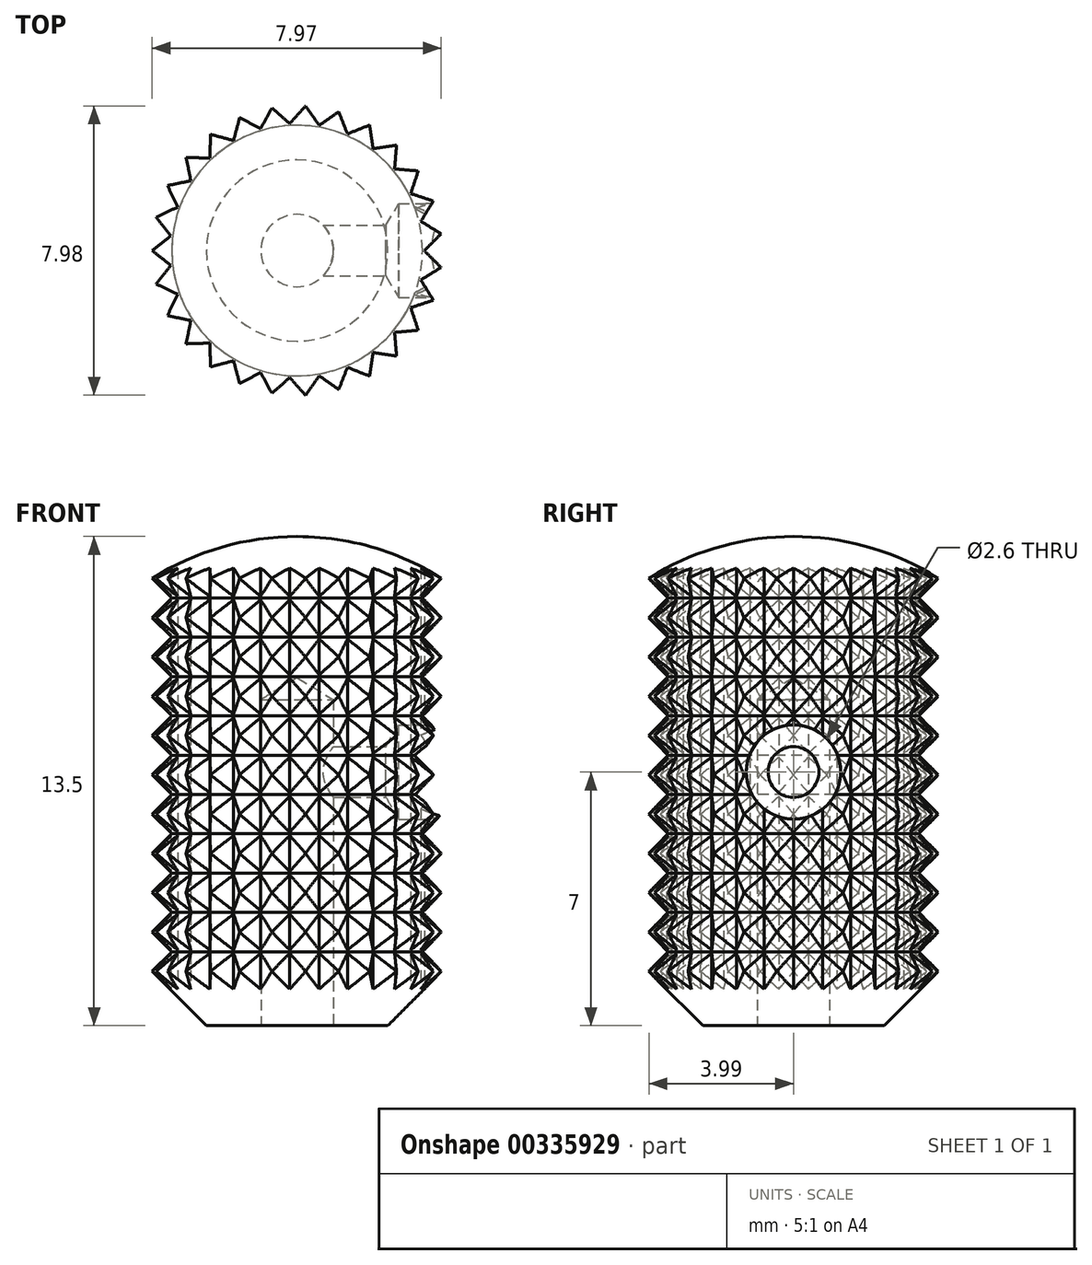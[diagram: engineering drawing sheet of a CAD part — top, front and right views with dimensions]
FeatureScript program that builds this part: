
annotation { "Feature Type Name" : "Feature", "Feature Type Description" : "" }
export const myFeature = defineFeature(function(context is Context, id is Id, definition is map)
    precondition{}
    {
        {
            var Q0;
            Q0=qCreatedBy(makeId("Top.planeOp"),FACE);
            var sketch = newSketch(context, id + "F0", { "sketchPlane" : qUnion([Q0])});
            skCircle(sketch, "E0", {"center": v(0, 0) * mm, "radius": 4 * mm, "construction": true});
            skLineSegment(sketch, "E1", {"start": v(0, 0) * mm, "end": v(4, 0) * mm, "construction": true});
            skLineSegment(sketch, "E2", {"start": v(3.5, 0) * mm, "end": v(3.97, 0.46) * mm});
            skLineSegment(sketch, "E3.MirrorCS", {"start": v(3.5, 0) * mm, "end": v(3.97, -0.46) * mm});
            skLineSegment(sketch, "E4.1.0", {"start": v(3.41, -0.8) * mm, "end": v(3.97, -0.46) * mm});
            skLineSegment(sketch, "E4.1.1", {"start": v(3.41, -0.8) * mm, "end": v(3.76, -1.37) * mm});
            skLineSegment(sketch, "E4.2.0", {"start": v(3.14, -1.57) * mm, "end": v(3.76, -1.37) * mm});
            skLineSegment(sketch, "E4.2.1", {"start": v(3.14, -1.57) * mm, "end": v(3.34, -2.2) * mm});
            skLineSegment(sketch, "E4.3.0", {"start": v(2.69, -2.26) * mm, "end": v(3.34, -2.2) * mm});
            skLineSegment(sketch, "E4.3.1", {"start": v(2.69, -2.26) * mm, "end": v(2.74, -2.9) * mm});
            skLineSegment(sketch, "E4.4.0", {"start": v(2.1, -2.81) * mm, "end": v(2.74, -2.9) * mm});
            skLineSegment(sketch, "E4.4.1", {"start": v(2.1, -2.81) * mm, "end": v(2, -3.46) * mm});
            skLineSegment(sketch, "E4.5.0", {"start": v(1.39, -3.22) * mm, "end": v(2, -3.46) * mm});
            skLineSegment(sketch, "E4.5.1", {"start": v(1.39, -3.22) * mm, "end": v(1.15, -3.83) * mm});
            skLineSegment(sketch, "E4.6.0", {"start": v(0.6, -3.46) * mm, "end": v(1.15, -3.83) * mm});
            skLineSegment(sketch, "E4.6.1", {"start": v(0.6, -3.46) * mm, "end": v(0.23, -4) * mm});
            skLineSegment(sketch, "E4.7.0", {"start": v(-0.2, -3.5) * mm, "end": v(0.23, -4) * mm});
            skLineSegment(sketch, "E4.7.1", {"start": v(-0.2, -3.5) * mm, "end": v(-0.7, -3.94) * mm});
            skLineSegment(sketch, "E4.8.0", {"start": v(-1, -3.36) * mm, "end": v(-0.7, -3.94) * mm});
            skLineSegment(sketch, "E4.8.1", {"start": v(-1, -3.36) * mm, "end": v(-1.58, -3.67) * mm});
            skLineSegment(sketch, "E4.9.0", {"start": v(-1.75, -3.04) * mm, "end": v(-1.58, -3.67) * mm});
            skLineSegment(sketch, "E4.9.1", {"start": v(-1.75, -3.04) * mm, "end": v(-2.39, -3.2) * mm});
            skLineSegment(sketch, "E4.10.0", {"start": v(-2.4, -2.55) * mm, "end": v(-2.39, -3.2) * mm});
            skLineSegment(sketch, "E4.10.1", {"start": v(-2.4, -2.55) * mm, "end": v(-3.06, -2.57) * mm});
            skLineSegment(sketch, "E4.11.0", {"start": v(-2.93, -1.93) * mm, "end": v(-3.06, -2.57) * mm});
            skLineSegment(sketch, "E4.11.1", {"start": v(-2.93, -1.93) * mm, "end": v(-3.57, -1.8) * mm});
            skLineSegment(sketch, "E4.12.0", {"start": v(-3.3, -1.2) * mm, "end": v(-3.57, -1.8) * mm});
            skLineSegment(sketch, "E4.12.1", {"start": v(-3.3, -1.2) * mm, "end": v(-3.9, -0.92) * mm});
            skLineSegment(sketch, "E4.13.0", {"start": v(-3.48, -0.4) * mm, "end": v(-3.9, -0.92) * mm});
            skLineSegment(sketch, "E4.13.1", {"start": v(-3.48, -0.4) * mm, "end": v(-4, 0) * mm});
            skLineSegment(sketch, "E4.14.0", {"start": v(-3.48, 0.4) * mm, "end": v(-4, 0) * mm});
            skLineSegment(sketch, "E4.14.1", {"start": v(-3.48, 0.4) * mm, "end": v(-3.9, 0.92) * mm});
            skLineSegment(sketch, "E4.15.0", {"start": v(-3.3, 1.2) * mm, "end": v(-3.9, 0.92) * mm});
            skLineSegment(sketch, "E4.15.1", {"start": v(-3.3, 1.2) * mm, "end": v(-3.57, 1.8) * mm});
            skLineSegment(sketch, "E4.16.0", {"start": v(-2.93, 1.93) * mm, "end": v(-3.57, 1.8) * mm});
            skLineSegment(sketch, "E4.16.1", {"start": v(-2.93, 1.93) * mm, "end": v(-3.06, 2.57) * mm});
            skLineSegment(sketch, "E4.17.0", {"start": v(-2.4, 2.55) * mm, "end": v(-3.06, 2.57) * mm});
            skLineSegment(sketch, "E4.17.1", {"start": v(-2.4, 2.55) * mm, "end": v(-2.39, 3.2) * mm});
            skLineSegment(sketch, "E4.18.0", {"start": v(-1.75, 3.04) * mm, "end": v(-2.39, 3.2) * mm});
            skLineSegment(sketch, "E4.18.1", {"start": v(-1.75, 3.04) * mm, "end": v(-1.58, 3.67) * mm});
            skLineSegment(sketch, "E4.19.0", {"start": v(-1, 3.36) * mm, "end": v(-1.58, 3.67) * mm});
            skLineSegment(sketch, "E4.19.1", {"start": v(-1, 3.36) * mm, "end": v(-0.7, 3.94) * mm});
            skLineSegment(sketch, "E4.20.0", {"start": v(-0.2, 3.5) * mm, "end": v(-0.7, 3.94) * mm});
            skLineSegment(sketch, "E4.20.1", {"start": v(-0.2, 3.5) * mm, "end": v(0.23, 4) * mm});
            skLineSegment(sketch, "E4.21.0", {"start": v(0.6, 3.46) * mm, "end": v(0.23, 4) * mm});
            skLineSegment(sketch, "E4.21.1", {"start": v(0.6, 3.46) * mm, "end": v(1.15, 3.83) * mm});
            skLineSegment(sketch, "E4.22.0", {"start": v(1.39, 3.22) * mm, "end": v(1.15, 3.83) * mm});
            skLineSegment(sketch, "E4.22.1", {"start": v(1.39, 3.22) * mm, "end": v(2, 3.46) * mm});
            skLineSegment(sketch, "E4.23.0", {"start": v(2.1, 2.81) * mm, "end": v(2, 3.46) * mm});
            skLineSegment(sketch, "E4.23.1", {"start": v(2.1, 2.81) * mm, "end": v(2.74, 2.9) * mm});
            skLineSegment(sketch, "E4.24.0", {"start": v(2.69, 2.26) * mm, "end": v(2.74, 2.9) * mm});
            skLineSegment(sketch, "E4.24.1", {"start": v(2.69, 2.26) * mm, "end": v(3.34, 2.2) * mm});
            skLineSegment(sketch, "E4.25.0", {"start": v(3.14, 1.57) * mm, "end": v(3.34, 2.2) * mm});
            skLineSegment(sketch, "E4.25.1", {"start": v(3.14, 1.57) * mm, "end": v(3.76, 1.37) * mm});
            skLineSegment(sketch, "E4.26.0", {"start": v(3.41, 0.8) * mm, "end": v(3.76, 1.37) * mm});
            skLineSegment(sketch, "E4.26.1", {"start": v(3.41, 0.8) * mm, "end": v(3.97, 0.46) * mm});
            skLineSegment(sketch, "E4.anchor1", {"start": v(0, 0) * mm, "end": v(3.5, 0) * mm, "construction": true});
            skLineSegment(sketch, "E4.anchor2", {"start": v(0, 0) * mm, "end": v(3.41, 0.8) * mm, "construction": true});
            skSolve(sketch);
        }
        {
            var Q0;
            Q0 = qSketchRegion(id + "F0", true);
            extrude(context, id + "F1", {"entities" : qUnion([Q0]), "depth" : 25 * mm});
        }
        {
            var Q0;
            Q0=qCreatedBy(makeId("Front.planeOp"),FACE);
            var sketch = newSketch(context, id + "F2", { "sketchPlane" : qUnion([Q0])});
            skLineSegment(sketch, "E5", {"start": v(0, 0) * mm, "end": v(-2.5, 0) * mm});
            skLineSegment(sketch, "E6", {"start": v(-2.5, 0) * mm, "end": v(-4, 1.5) * mm});
            skLineSegment(sketch, "E7", {"start": v(-4, 1.5) * mm, "end": v(-4, 12.34) * mm});
            skLineSegment(sketch, "E8.MirrorCS", {"start": v(4, 1.5) * mm, "end": v(4, 12.34) * mm});
            skLineSegment(sketch, "E9.MirrorCS", {"start": v(2.5, 0) * mm, "end": v(4, 1.5) * mm});
            skLineSegment(sketch, "E10.MirrorCS", {"start": v(0, 0) * mm, "end": v(2.5, 0) * mm});
            skArc(sketch, "E11", {"start": v(-4, 12.34) * mm, "mid": v(0, 13.5) * mm, "end": v(4, 12.34) * mm});
            skPoint(sketch, "E12", {"position": v(0, 13.5) * mm});
            skLineSegment(sketch, "E13", {"start": v(-4, 1.5) * mm, "end": v(-3.46, 2.04) * mm});
            skLineSegment(sketch, "E14", {"start": v(-3.46, 2.04) * mm, "end": v(-4, 2.58) * mm});
            skLineSegment(sketch, "E15.1.0.0", {"start": v(-4, 2.58) * mm, "end": v(-3.46, 3.13) * mm});
            skLineSegment(sketch, "E15.1.0.1", {"start": v(-3.46, 3.13) * mm, "end": v(-4, 3.67) * mm});
            skLineSegment(sketch, "E15.2.0.0", {"start": v(-4, 3.67) * mm, "end": v(-3.46, 4.21) * mm});
            skLineSegment(sketch, "E15.2.0.1", {"start": v(-3.46, 4.21) * mm, "end": v(-4, 4.75) * mm});
            skLineSegment(sketch, "E15.3.0.0", {"start": v(-4, 4.75) * mm, "end": v(-3.46, 5.3) * mm});
            skLineSegment(sketch, "E15.3.0.1", {"start": v(-3.46, 5.3) * mm, "end": v(-4, 5.84) * mm});
            skLineSegment(sketch, "E15.4.0.0", {"start": v(-4, 5.84) * mm, "end": v(-3.46, 6.38) * mm});
            skLineSegment(sketch, "E15.4.0.1", {"start": v(-3.46, 6.38) * mm, "end": v(-4, 6.92) * mm});
            skLineSegment(sketch, "E15.5.0.0", {"start": v(-4, 6.92) * mm, "end": v(-3.46, 7.46) * mm});
            skLineSegment(sketch, "E15.5.0.1", {"start": v(-3.46, 7.46) * mm, "end": v(-4, 8) * mm});
            skLineSegment(sketch, "E15.6.0.0", {"start": v(-4, 8) * mm, "end": v(-3.46, 8.55) * mm});
            skLineSegment(sketch, "E15.6.0.1", {"start": v(-3.46, 8.55) * mm, "end": v(-4, 9.1) * mm});
            skLineSegment(sketch, "E15.7.0.0", {"start": v(-4, 9.1) * mm, "end": v(-3.46, 9.63) * mm});
            skLineSegment(sketch, "E15.7.0.1", {"start": v(-3.46, 9.63) * mm, "end": v(-4, 10.18) * mm});
            skLineSegment(sketch, "E15.8.0.0", {"start": v(-4, 10.18) * mm, "end": v(-3.46, 10.72) * mm});
            skLineSegment(sketch, "E15.8.0.1", {"start": v(-3.46, 10.72) * mm, "end": v(-4, 11.26) * mm});
            skLineSegment(sketch, "E15.9.0.0", {"start": v(-4, 11.26) * mm, "end": v(-3.46, 11.8) * mm});
            skLineSegment(sketch, "E15.9.0.1", {"start": v(-3.46, 11.8) * mm, "end": v(-4, 12.34) * mm});
            skLineSegment(sketch, "E15.direction1", {"start": v(-4, 1.5) * mm, "end": v(-4, 2.58) * mm, "construction": true});
            skLineSegment(sketch, "E16", {"start": v(0, 13.5) * mm, "end": v(0, 0) * mm});
            skSolve(sketch);
        }
        {
            var Q0;
            Q0=makeQuery(id+"F2.imprint","IMPRINT",FACE,{"disambiguationData":[TD([[makeQuery(id+"F2.imprint","IMPRINT",EDGE,{"derivedFrom":sQuery(id+"F2.wireOp",EDGE,"E5")}),-1.0]])]});
            var Q1;
            Q1=sQuery(id+"F2.wireOp",EDGE,"E16");
            revolve(context, id + "F3", {"entities" : qUnion([Q0]), "axis" : qUnion([Q1]), "revolveType" : RevolveType.FULL});
        }
        {
            var Q0;
            Q0=makeQuery(id+"F1.opExtrude","SWEPT_BODY",BODY,{"disambiguationData":[OSD([sQuery(id+"F0.wireOp",EDGE,"E2"),sQuery(id+"F0.wireOp",EDGE,"E3.MirrorCS"),sQuery(id+"F0.wireOp",EDGE,"E4.1.0"),sQuery(id+"F0.wireOp",EDGE,"E4.1.1"),sQuery(id+"F0.wireOp",EDGE,"E4.2.0"),sQuery(id+"F0.wireOp",EDGE,"E4.2.1"),sQuery(id+"F0.wireOp",EDGE,"E4.3.0"),sQuery(id+"F0.wireOp",EDGE,"E4.3.1"),sQuery(id+"F0.wireOp",EDGE,"E4.4.0"),sQuery(id+"F0.wireOp",EDGE,"E4.4.1"),sQuery(id+"F0.wireOp",EDGE,"E4.5.0"),sQuery(id+"F0.wireOp",EDGE,"E4.5.1"),sQuery(id+"F0.wireOp",EDGE,"E4.6.0"),sQuery(id+"F0.wireOp",EDGE,"E4.6.1"),sQuery(id+"F0.wireOp",EDGE,"E4.7.0"),sQuery(id+"F0.wireOp",EDGE,"E4.7.1"),sQuery(id+"F0.wireOp",EDGE,"E4.8.0"),sQuery(id+"F0.wireOp",EDGE,"E4.8.1"),sQuery(id+"F0.wireOp",EDGE,"E4.9.0"),sQuery(id+"F0.wireOp",EDGE,"E4.9.1"),sQuery(id+"F0.wireOp",EDGE,"E4.10.0"),sQuery(id+"F0.wireOp",EDGE,"E4.10.1"),sQuery(id+"F0.wireOp",EDGE,"E4.11.0"),sQuery(id+"F0.wireOp",EDGE,"E4.11.1"),sQuery(id+"F0.wireOp",EDGE,"E4.12.0"),sQuery(id+"F0.wireOp",EDGE,"E4.12.1"),sQuery(id+"F0.wireOp",EDGE,"E4.13.0"),sQuery(id+"F0.wireOp",EDGE,"E4.13.1"),sQuery(id+"F0.wireOp",EDGE,"E4.14.0"),sQuery(id+"F0.wireOp",EDGE,"E4.14.1"),sQuery(id+"F0.wireOp",EDGE,"E4.15.0"),sQuery(id+"F0.wireOp",EDGE,"E4.15.1"),sQuery(id+"F0.wireOp",EDGE,"E4.16.0"),sQuery(id+"F0.wireOp",EDGE,"E4.16.1"),sQuery(id+"F0.wireOp",EDGE,"E4.17.0"),sQuery(id+"F0.wireOp",EDGE,"E4.17.1"),sQuery(id+"F0.wireOp",EDGE,"E4.18.0"),sQuery(id+"F0.wireOp",EDGE,"E4.18.1"),sQuery(id+"F0.wireOp",EDGE,"E4.19.0"),sQuery(id+"F0.wireOp",EDGE,"E4.19.1"),sQuery(id+"F0.wireOp",EDGE,"E4.20.0"),sQuery(id+"F0.wireOp",EDGE,"E4.20.1"),sQuery(id+"F0.wireOp",EDGE,"E4.21.0"),sQuery(id+"F0.wireOp",EDGE,"E4.21.1"),sQuery(id+"F0.wireOp",EDGE,"E4.22.0"),sQuery(id+"F0.wireOp",EDGE,"E4.22.1"),sQuery(id+"F0.wireOp",EDGE,"E4.23.0"),sQuery(id+"F0.wireOp",EDGE,"E4.23.1"),sQuery(id+"F0.wireOp",EDGE,"E4.24.0"),sQuery(id+"F0.wireOp",EDGE,"E4.24.1"),sQuery(id+"F0.wireOp",EDGE,"E4.25.0"),sQuery(id+"F0.wireOp",EDGE,"E4.25.1"),sQuery(id+"F0.wireOp",EDGE,"E4.26.0"),sQuery(id+"F0.wireOp",EDGE,"E4.26.1")])]});
            var Q1;
            Q1=makeQuery(id+"F3.opRevolve","SWEPT_BODY",BODY,{"disambiguationData":[OSD([sQuery(id+"F2.wireOp",EDGE,"E5"),sQuery(id+"F2.wireOp",EDGE,"E6"),sQuery(id+"F2.wireOp",EDGE,"E11"),sQuery(id+"F2.wireOp",EDGE,"E13"),sQuery(id+"F2.wireOp",EDGE,"E14"),sQuery(id+"F2.wireOp",EDGE,"E15.1.0.0"),sQuery(id+"F2.wireOp",EDGE,"E15.1.0.1"),sQuery(id+"F2.wireOp",EDGE,"E15.2.0.0"),sQuery(id+"F2.wireOp",EDGE,"E15.2.0.1"),sQuery(id+"F2.wireOp",EDGE,"E15.3.0.0"),sQuery(id+"F2.wireOp",EDGE,"E15.3.0.1"),sQuery(id+"F2.wireOp",EDGE,"E15.4.0.0"),sQuery(id+"F2.wireOp",EDGE,"E15.4.0.1"),sQuery(id+"F2.wireOp",EDGE,"E15.5.0.0"),sQuery(id+"F2.wireOp",EDGE,"E15.5.0.1"),sQuery(id+"F2.wireOp",EDGE,"E15.6.0.0"),sQuery(id+"F2.wireOp",EDGE,"E15.6.0.1"),sQuery(id+"F2.wireOp",EDGE,"E15.7.0.0"),sQuery(id+"F2.wireOp",EDGE,"E15.7.0.1"),sQuery(id+"F2.wireOp",EDGE,"E15.8.0.0"),sQuery(id+"F2.wireOp",EDGE,"E15.8.0.1"),sQuery(id+"F2.wireOp",EDGE,"E15.9.0.0"),sQuery(id+"F2.wireOp",EDGE,"E15.9.0.1"),sQuery(id+"F2.wireOp",EDGE,"E16")])]});
            booleanBodies(context, id + "F4", {"operationType" : BooleanOperationType.INTERSECTION, "tools" : qUnion([Q0, Q1])});
        }
        {
            var Q0;
            Q0=makeQuery(id+"F1.opExtrude","CAP_FACE",FACE,{"disambiguationData":[OSD([sQuery(id+"F0.wireOp",EDGE,"E2"),sQuery(id+"F0.wireOp",EDGE,"E3.MirrorCS"),sQuery(id+"F0.wireOp",EDGE,"E4.1.0"),sQuery(id+"F0.wireOp",EDGE,"E4.1.1"),sQuery(id+"F0.wireOp",EDGE,"E4.2.0"),sQuery(id+"F0.wireOp",EDGE,"E4.2.1"),sQuery(id+"F0.wireOp",EDGE,"E4.3.0"),sQuery(id+"F0.wireOp",EDGE,"E4.3.1"),sQuery(id+"F0.wireOp",EDGE,"E4.4.0"),sQuery(id+"F0.wireOp",EDGE,"E4.4.1"),sQuery(id+"F0.wireOp",EDGE,"E4.5.0"),sQuery(id+"F0.wireOp",EDGE,"E4.5.1"),sQuery(id+"F0.wireOp",EDGE,"E4.6.0"),sQuery(id+"F0.wireOp",EDGE,"E4.6.1"),sQuery(id+"F0.wireOp",EDGE,"E4.7.0"),sQuery(id+"F0.wireOp",EDGE,"E4.7.1"),sQuery(id+"F0.wireOp",EDGE,"E4.8.0"),sQuery(id+"F0.wireOp",EDGE,"E4.8.1"),sQuery(id+"F0.wireOp",EDGE,"E4.9.0"),sQuery(id+"F0.wireOp",EDGE,"E4.9.1"),sQuery(id+"F0.wireOp",EDGE,"E4.10.0"),sQuery(id+"F0.wireOp",EDGE,"E4.10.1"),sQuery(id+"F0.wireOp",EDGE,"E4.11.0"),sQuery(id+"F0.wireOp",EDGE,"E4.11.1"),sQuery(id+"F0.wireOp",EDGE,"E4.12.0"),sQuery(id+"F0.wireOp",EDGE,"E4.12.1"),sQuery(id+"F0.wireOp",EDGE,"E4.13.0"),sQuery(id+"F0.wireOp",EDGE,"E4.13.1"),sQuery(id+"F0.wireOp",EDGE,"E4.14.0"),sQuery(id+"F0.wireOp",EDGE,"E4.14.1"),sQuery(id+"F0.wireOp",EDGE,"E4.15.0"),sQuery(id+"F0.wireOp",EDGE,"E4.15.1"),sQuery(id+"F0.wireOp",EDGE,"E4.16.0"),sQuery(id+"F0.wireOp",EDGE,"E4.16.1"),sQuery(id+"F0.wireOp",EDGE,"E4.17.0"),sQuery(id+"F0.wireOp",EDGE,"E4.17.1"),sQuery(id+"F0.wireOp",EDGE,"E4.18.0"),sQuery(id+"F0.wireOp",EDGE,"E4.18.1"),sQuery(id+"F0.wireOp",EDGE,"E4.19.0"),sQuery(id+"F0.wireOp",EDGE,"E4.19.1"),sQuery(id+"F0.wireOp",EDGE,"E4.20.0"),sQuery(id+"F0.wireOp",EDGE,"E4.20.1"),sQuery(id+"F0.wireOp",EDGE,"E4.21.0"),sQuery(id+"F0.wireOp",EDGE,"E4.21.1"),sQuery(id+"F0.wireOp",EDGE,"E4.22.0"),sQuery(id+"F0.wireOp",EDGE,"E4.22.1"),sQuery(id+"F0.wireOp",EDGE,"E4.23.0"),sQuery(id+"F0.wireOp",EDGE,"E4.23.1"),sQuery(id+"F0.wireOp",EDGE,"E4.24.0"),sQuery(id+"F0.wireOp",EDGE,"E4.24.1"),sQuery(id+"F0.wireOp",EDGE,"E4.25.0"),sQuery(id+"F0.wireOp",EDGE,"E4.25.1"),sQuery(id+"F0.wireOp",EDGE,"E4.26.0"),sQuery(id+"F0.wireOp",EDGE,"E4.26.1")])],"isStart":true});
            var sketch = newSketch(context, id + "F5", { "sketchPlane" : qUnion([Q0])});
            skPoint(sketch, "E17", {"position": v(0, 0) * mm});
            skSolve(sketch);
        }
        {
            var Q0;
            Q0=sQuery(id+"F5.wireOp",VERTEX,"E17");
            var Q1;
            Q1=makeQuery(id+"F4.opBoolean","INTERSECT",BODY,{"derivedFrom":[makeQuery(id+"F1.opExtrude","SWEPT_BODY",BODY,{"disambiguationData":[OSD([sQuery(id+"F0.wireOp",EDGE,"E2"),sQuery(id+"F0.wireOp",EDGE,"E3.MirrorCS"),sQuery(id+"F0.wireOp",EDGE,"E4.1.0"),sQuery(id+"F0.wireOp",EDGE,"E4.1.1"),sQuery(id+"F0.wireOp",EDGE,"E4.2.0"),sQuery(id+"F0.wireOp",EDGE,"E4.2.1"),sQuery(id+"F0.wireOp",EDGE,"E4.3.0"),sQuery(id+"F0.wireOp",EDGE,"E4.3.1"),sQuery(id+"F0.wireOp",EDGE,"E4.4.0"),sQuery(id+"F0.wireOp",EDGE,"E4.4.1"),sQuery(id+"F0.wireOp",EDGE,"E4.5.0"),sQuery(id+"F0.wireOp",EDGE,"E4.5.1"),sQuery(id+"F0.wireOp",EDGE,"E4.6.0"),sQuery(id+"F0.wireOp",EDGE,"E4.6.1"),sQuery(id+"F0.wireOp",EDGE,"E4.7.0"),sQuery(id+"F0.wireOp",EDGE,"E4.7.1"),sQuery(id+"F0.wireOp",EDGE,"E4.8.0"),sQuery(id+"F0.wireOp",EDGE,"E4.8.1"),sQuery(id+"F0.wireOp",EDGE,"E4.9.0"),sQuery(id+"F0.wireOp",EDGE,"E4.9.1"),sQuery(id+"F0.wireOp",EDGE,"E4.10.0"),sQuery(id+"F0.wireOp",EDGE,"E4.10.1"),sQuery(id+"F0.wireOp",EDGE,"E4.11.0"),sQuery(id+"F0.wireOp",EDGE,"E4.11.1"),sQuery(id+"F0.wireOp",EDGE,"E4.12.0"),sQuery(id+"F0.wireOp",EDGE,"E4.12.1"),sQuery(id+"F0.wireOp",EDGE,"E4.13.0"),sQuery(id+"F0.wireOp",EDGE,"E4.13.1"),sQuery(id+"F0.wireOp",EDGE,"E4.14.0"),sQuery(id+"F0.wireOp",EDGE,"E4.14.1"),sQuery(id+"F0.wireOp",EDGE,"E4.15.0"),sQuery(id+"F0.wireOp",EDGE,"E4.15.1"),sQuery(id+"F0.wireOp",EDGE,"E4.16.0"),sQuery(id+"F0.wireOp",EDGE,"E4.16.1"),sQuery(id+"F0.wireOp",EDGE,"E4.17.0"),sQuery(id+"F0.wireOp",EDGE,"E4.17.1"),sQuery(id+"F0.wireOp",EDGE,"E4.18.0"),sQuery(id+"F0.wireOp",EDGE,"E4.18.1"),sQuery(id+"F0.wireOp",EDGE,"E4.19.0"),sQuery(id+"F0.wireOp",EDGE,"E4.19.1"),sQuery(id+"F0.wireOp",EDGE,"E4.20.0"),sQuery(id+"F0.wireOp",EDGE,"E4.20.1"),sQuery(id+"F0.wireOp",EDGE,"E4.21.0"),sQuery(id+"F0.wireOp",EDGE,"E4.21.1"),sQuery(id+"F0.wireOp",EDGE,"E4.22.0"),sQuery(id+"F0.wireOp",EDGE,"E4.22.1"),sQuery(id+"F0.wireOp",EDGE,"E4.23.0"),sQuery(id+"F0.wireOp",EDGE,"E4.23.1"),sQuery(id+"F0.wireOp",EDGE,"E4.24.0"),sQuery(id+"F0.wireOp",EDGE,"E4.24.1"),sQuery(id+"F0.wireOp",EDGE,"E4.25.0"),sQuery(id+"F0.wireOp",EDGE,"E4.25.1"),sQuery(id+"F0.wireOp",EDGE,"E4.26.0"),sQuery(id+"F0.wireOp",EDGE,"E4.26.1")])]}),makeQuery(id+"F3.opRevolve","SWEPT_BODY",BODY,{"disambiguationData":[OSD([sQuery(id+"F2.wireOp",EDGE,"E5"),sQuery(id+"F2.wireOp",EDGE,"E6"),sQuery(id+"F2.wireOp",EDGE,"E11"),sQuery(id+"F2.wireOp",EDGE,"E13"),sQuery(id+"F2.wireOp",EDGE,"E14"),sQuery(id+"F2.wireOp",EDGE,"E15.1.0.0"),sQuery(id+"F2.wireOp",EDGE,"E15.1.0.1"),sQuery(id+"F2.wireOp",EDGE,"E15.2.0.0"),sQuery(id+"F2.wireOp",EDGE,"E15.2.0.1"),sQuery(id+"F2.wireOp",EDGE,"E15.3.0.0"),sQuery(id+"F2.wireOp",EDGE,"E15.3.0.1"),sQuery(id+"F2.wireOp",EDGE,"E15.4.0.0"),sQuery(id+"F2.wireOp",EDGE,"E15.4.0.1"),sQuery(id+"F2.wireOp",EDGE,"E15.5.0.0"),sQuery(id+"F2.wireOp",EDGE,"E15.5.0.1"),sQuery(id+"F2.wireOp",EDGE,"E15.6.0.0"),sQuery(id+"F2.wireOp",EDGE,"E15.6.0.1"),sQuery(id+"F2.wireOp",EDGE,"E15.7.0.0"),sQuery(id+"F2.wireOp",EDGE,"E15.7.0.1"),sQuery(id+"F2.wireOp",EDGE,"E15.8.0.0"),sQuery(id+"F2.wireOp",EDGE,"E15.8.0.1"),sQuery(id+"F2.wireOp",EDGE,"E15.9.0.0"),sQuery(id+"F2.wireOp",EDGE,"E15.9.0.1"),sQuery(id+"F2.wireOp",EDGE,"E16")])]})]});
            hole(context, id + "F6", {"style" : HoleStyle.SIMPLE, "endStyle" : HoleEndStyle.BLIND, "holeDiameter" : 2 * mm, "holeDepth" : 9 * mm, "tappedDepth" : 12 * mm, "tapClearance" : 3, "locations" : qUnion([Q0]), "scope" : qUnion([Q1])});
        }
        {
            var Q0;
            Q0=qCreatedBy(makeId("Front.planeOp"),FACE);
            var sketch = newSketch(context, id + "F7", { "sketchPlane" : qUnion([Q0])});
            skLineSegment(sketch, "E18.0", {"start": v(0, 13.5) * mm, "end": v(0, 0) * mm, "construction": true});
            skLineSegment(sketch, "E19.0", {"start": v(4, 1.5) * mm, "end": v(4, 12.34) * mm, "construction": true});
            skLineSegment(sketch, "E20", {"start": v(0, 7) * mm, "end": v(4, 7) * mm, "construction": true});
            skLineSegment(sketch, "E21.bottom", {"start": v(0, 7.7) * mm, "end": v(4, 7.7) * mm});
            skLineSegment(sketch, "E21.top", {"start": v(0, 6.3) * mm, "end": v(4, 6.3) * mm});
            skLineSegment(sketch, "E21.left", {"start": v(0, 7.7) * mm, "end": v(0, 6.3) * mm});
            skLineSegment(sketch, "E21.right", {"start": v(4, 7.7) * mm, "end": v(4, 6.3) * mm});
            skPoint(sketch, "E22", {"position": v(0, 7) * mm});
            skLineSegment(sketch, "E23.bottom", {"start": v(2.8, 8.3) * mm, "end": v(4, 8.3) * mm});
            skLineSegment(sketch, "E23.top", {"start": v(2.8, 5.7) * mm, "end": v(4, 5.7) * mm});
            skLineSegment(sketch, "E23.left", {"start": v(2.8, 8.3) * mm, "end": v(2.8, 5.7) * mm});
            skLineSegment(sketch, "E23.right", {"start": v(4, 8.3) * mm, "end": v(4, 5.7) * mm});
            skPoint(sketch, "E24", {"position": v(2.8, 7) * mm});
            skLineSegment(sketch, "E25", {"start": v(0, 7) * mm, "end": v(4, 7) * mm});
            skLineSegment(sketch, "E26", {"start": v(2.8, 8.3) * mm, "end": v(2.45, 7.7) * mm});
            skLineSegment(sketch, "E27.MirrorCS", {"start": v(2.8, 5.7) * mm, "end": v(2.45, 6.3) * mm});
            skSolve(sketch);
        }
        {
            var Q0;
            {var subQ1=sQuery(id+"F7.wireOp",EDGE,"E21.bottom");var subQ5=sQuery(id+"F7.wireOp",EDGE,"E21.left");var subQ6=makeQuery(id+"F7.imprint","INTERSECT",VERTEX,{"derivedFrom":[subQ1,subQ5]});Q0=makeQuery(id+"F7.imprint","IMPRINT",FACE,{"disambiguationData":[TD([[makeQuery(id+"F7.imprint","IMPRINT",EDGE,{"disambiguationData":[TD([[subQ6,-1.0]])],"derivedFrom":subQ1}),-1.0]])]});}
            var Q1;
            {var subQ0=sQuery(id+"F7.wireOp",EDGE,"E23.right");var subQ1=sQuery(id+"F7.wireOp",EDGE,"E21.bottom");var subQ2=makeQuery(id+"F7.imprint","INTERSECT",VERTEX,{"derivedFrom":[subQ1,subQ0]});Q1=makeQuery(id+"F7.imprint","IMPRINT",FACE,{"disambiguationData":[TD([[makeQuery(id+"F7.imprint","IMPRINT",EDGE,{"disambiguationData":[TD([[subQ2,1.0]])],"derivedFrom":subQ1}),-1.0]])]});}
            var Q2;
            {var subQ0=sQuery(id+"F7.wireOp",EDGE,"E26");Q2=makeQuery(id+"F7.imprint","IMPRINT",FACE,{"disambiguationData":[TD([[makeQuery(id+"F7.imprint","IMPRINT",EDGE,{"derivedFrom":subQ0}),1.0]])]});}
            var Q3;
            {var subQ5=sQuery(id+"F7.wireOp",EDGE,"E23.bottom");Q3=makeQuery(id+"F7.imprint","IMPRINT",FACE,{"disambiguationData":[TD([[makeQuery(id+"F7.imprint","IMPRINT",EDGE,{"derivedFrom":subQ5}),-1.0]])]});}
            var Q4;
            Q4=sQuery(id+"F7.wireOp",EDGE,"E25");
            revolve(context, id + "F8", {"operationType" : NewBodyOperationType.REMOVE, "entities" : qUnion([Q0, Q1, Q2, Q3]), "axis" : qUnion([Q4]), "revolveType" : RevolveType.FULL, "oppositeDirection" : true});
        }
    });
